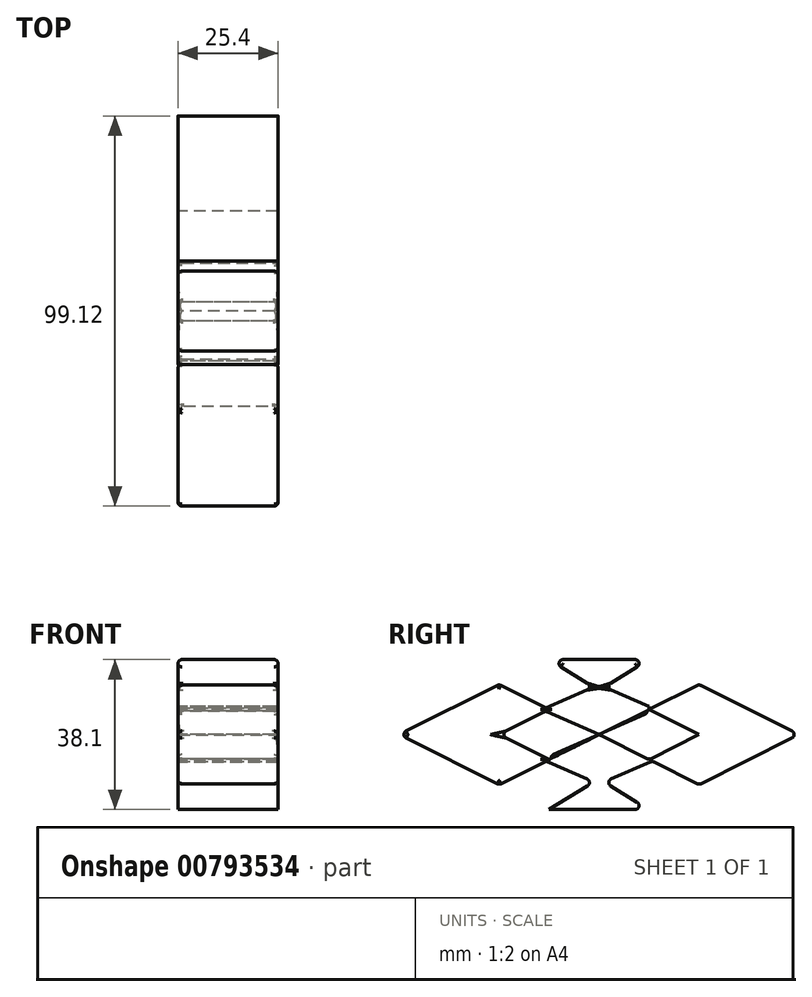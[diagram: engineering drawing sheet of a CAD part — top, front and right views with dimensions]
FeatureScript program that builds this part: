
annotation { "Feature Type Name" : "Feature", "Feature Type Description" : "" }
export const myFeature = defineFeature(function(context is Context, id is Id, definition is map)
    precondition{}
    {
        {
            var Q0;
            Q0=qCreatedBy(makeId("Right.planeOp"),FACE);
            var sketch = newSketch(context, id + "F0", { "sketchPlane" : qUnion([Q0])});
            skLineSegment(sketch, "E0", {"start": v(-25.4, 0) * mm, "end": v(-25.4, 12.7) * mm});
            skLineSegment(sketch, "E1.MirrorCS", {"start": v(-25.4, 0) * mm, "end": v(-25.4, -12.7) * mm});
            skLineSegment(sketch, "E2.1.0.0", {"start": v(0, 0) * mm, "end": v(0, 12.7) * mm});
            skLineSegment(sketch, "E2.1.0.1", {"start": v(0, 0) * mm, "end": v(0, -12.7) * mm});
            skLineSegment(sketch, "E2.2.0.0", {"start": v(25.4, 0) * mm, "end": v(25.4, 12.7) * mm});
            skLineSegment(sketch, "E2.2.0.1", {"start": v(25.4, 0) * mm, "end": v(25.4, -12.7) * mm});
            skLineSegment(sketch, "E3", {"start": v(-25.4, 12.7) * mm, "end": v(25.4, -12.7) * mm});
            skLineSegment(sketch, "E4", {"start": v(25.4, 12.7) * mm, "end": v(-25.4, -12.7) * mm});
            skLineSegment(sketch, "E5", {"start": v(-25.4, 0) * mm, "end": v(0, 12.7) * mm});
            skLineSegment(sketch, "E6", {"start": v(0, 12.7) * mm, "end": v(25.4, 0) * mm});
            skLineSegment(sketch, "E7", {"start": v(25.4, 0) * mm, "end": v(0, -12.7) * mm});
            skLineSegment(sketch, "E8", {"start": v(0, -12.7) * mm, "end": v(-25.4, 0) * mm});
            skLineSegment(sketch, "E9", {"start": v(-12.7, 6.35) * mm, "end": v(-12.7, 19.05) * mm});
            skLineSegment(sketch, "E10", {"start": v(12.7, 6.35) * mm, "end": v(12.7, 19.05) * mm});
            skLineSegment(sketch, "E11.MirrorCS", {"start": v(-12.7, -6.35) * mm, "end": v(-12.7, -19.05) * mm});
            skLineSegment(sketch, "E12.MirrorCS", {"start": v(12.7, -6.35) * mm, "end": v(12.7, -19.05) * mm});
            skLineSegment(sketch, "E13", {"start": v(-12.7, 19.05) * mm, "end": v(-25.4, 12.7) * mm});
            skLineSegment(sketch, "E14", {"start": v(-25.4, -12.7) * mm, "end": v(-12.7, -19.05) * mm});
            skLineSegment(sketch, "E15", {"start": v(12.7, -19.05) * mm, "end": v(25.4, -12.7) * mm});
            skLineSegment(sketch, "E16", {"start": v(12.7, 19.05) * mm, "end": v(25.4, 12.7) * mm});
            skLineSegment(sketch, "E17", {"start": v(-12.7, 19.05) * mm, "end": v(12.7, 19.05) * mm});
            skLineSegment(sketch, "E18", {"start": v(0, 12.7) * mm, "end": v(-12.7, 19.05) * mm});
            skLineSegment(sketch, "E19", {"start": v(0, 12.7) * mm, "end": v(12.7, 19.05) * mm});
            skLineSegment(sketch, "E20", {"start": v(0, -12.7) * mm, "end": v(-12.7, -19.05) * mm});
            skLineSegment(sketch, "E21", {"start": v(0, -12.7) * mm, "end": v(12.7, -19.05) * mm});
            skLineSegment(sketch, "E22", {"start": v(12.7, -19.05) * mm, "end": v(-12.7, -19.05) * mm});
            skLineSegment(sketch, "E23", {"start": v(-25.4, 12.7) * mm, "end": v(-50.8, 0) * mm});
            skLineSegment(sketch, "E24", {"start": v(-50.8, 0) * mm, "end": v(-25.4, -12.7) * mm});
            skLineSegment(sketch, "E25", {"start": v(25.4, 12.7) * mm, "end": v(50.8, 0) * mm});
            skLineSegment(sketch, "E26", {"start": v(50.8, 0) * mm, "end": v(25.4, -12.7) * mm});
            skLineSegment(sketch, "E27", {"start": v(50.8, 0) * mm, "end": v(-50.8, 0) * mm});
            skLineSegment(sketch, "E28", {"start": v(12.7, 19.05) * mm, "end": v(1.3, 12.05) * mm});
            skLineSegment(sketch, "E29.MirrorCS", {"start": v(-12.7, 19.05) * mm, "end": v(-1.3, 12.05) * mm});
            skLineSegment(sketch, "E30.MirrorCS", {"start": v(12.7, -19.05) * mm, "end": v(1.3, -12.05) * mm});
            skLineSegment(sketch, "E31.MirrorCS", {"start": v(-12.7, -19.05) * mm, "end": v(-1.3, -12.05) * mm});
            skLineSegment(sketch, "E32", {"start": v(0, 0) * mm, "end": v(13.53, 5.93) * mm});
            skLineSegment(sketch, "E33", {"start": v(1.3, 12.05) * mm, "end": v(13.53, 6.77) * mm});
            skLineSegment(sketch, "E34.MirrorCS", {"start": v(-1.3, 12.05) * mm, "end": v(-13.53, 6.77) * mm});
            skLineSegment(sketch, "E35.MirrorCS", {"start": v(0, 0) * mm, "end": v(-13.53, 5.93) * mm});
            skLineSegment(sketch, "E36.MirrorCS", {"start": v(0, 0) * mm, "end": v(13.53, -5.93) * mm});
            skLineSegment(sketch, "E37.MirrorCS", {"start": v(1.3, -12.05) * mm, "end": v(13.53, -6.77) * mm});
            skLineSegment(sketch, "E38.MirrorCS", {"start": v(0, 0) * mm, "end": v(-13.53, -5.93) * mm});
            skLineSegment(sketch, "E39.MirrorCS", {"start": v(-1.3, -12.05) * mm, "end": v(-13.53, -6.77) * mm});
            skSolve(sketch);
        }
        {
            var Q0;
            {var subQ0=sQuery(id+"F0.wireOp",EDGE,"E1.MirrorCS");Q0=makeQuery(id+"F0.imprint","IMPRINT",FACE,{"disambiguationData":[TD([[makeQuery(id+"F0.imprint","IMPRINT",EDGE,{"derivedFrom":subQ0}),-1.0]])]});}
            var Q1;
            {var subQ0=sQuery(id+"F0.wireOp",EDGE,"E2.2.0.0");Q1=makeQuery(id+"F0.imprint","IMPRINT",FACE,{"disambiguationData":[TD([[makeQuery(id+"F0.imprint","IMPRINT",EDGE,{"derivedFrom":subQ0}),-1.0]])]});}
            var Q2;
            {var subQ0=sQuery(id+"F0.wireOp",EDGE,"E2.2.0.0");Q2=makeQuery(id+"F0.imprint","IMPRINT",FACE,{"disambiguationData":[TD([[makeQuery(id+"F0.imprint","IMPRINT",EDGE,{"derivedFrom":subQ0}),1.0]])]});}
            var Q3;
            {var subQ0=sQuery(id+"F0.wireOp",EDGE,"E2.1.0.0");Q3=makeQuery(id+"F0.imprint","IMPRINT",FACE,{"disambiguationData":[TD([[makeQuery(id+"F0.imprint","IMPRINT",EDGE,{"derivedFrom":subQ0}),-1.0]])]});}
            var Q4;
            {var subQ0=sQuery(id+"F0.wireOp",EDGE,"E2.1.0.0");Q4=makeQuery(id+"F0.imprint","IMPRINT",FACE,{"disambiguationData":[TD([[makeQuery(id+"F0.imprint","IMPRINT",EDGE,{"derivedFrom":subQ0}),1.0]])]});}
            var Q5;
            {var subQ0=sQuery(id+"F0.wireOp",EDGE,"E0");Q5=makeQuery(id+"F0.imprint","IMPRINT",FACE,{"disambiguationData":[TD([[makeQuery(id+"F0.imprint","IMPRINT",EDGE,{"derivedFrom":subQ0}),-1.0]])]});}
            var Q6;
            {var subQ0=sQuery(id+"F0.wireOp",EDGE,"E1.MirrorCS");Q6=makeQuery(id+"F0.imprint","IMPRINT",FACE,{"disambiguationData":[TD([[makeQuery(id+"F0.imprint","IMPRINT",EDGE,{"derivedFrom":subQ0}),1.0]])]});}
            var Q7;
            {var subQ0=sQuery(id+"F0.wireOp",EDGE,"E2.1.0.1");Q7=makeQuery(id+"F0.imprint","IMPRINT",FACE,{"disambiguationData":[TD([[makeQuery(id+"F0.imprint","IMPRINT",EDGE,{"derivedFrom":subQ0}),1.0]])]});}
            var Q8;
            {var subQ0=sQuery(id+"F0.wireOp",EDGE,"E2.2.0.1");Q8=makeQuery(id+"F0.imprint","IMPRINT",FACE,{"disambiguationData":[TD([[makeQuery(id+"F0.imprint","IMPRINT",EDGE,{"derivedFrom":subQ0}),-1.0]])]});}
            var Q9;
            Q9=makeQuery(id+"F0.imprint","IMPRINT",FACE,{"disambiguationData":[TD([[makeQuery(id+"F0.imprint","IMPRINT",EDGE,{"derivedFrom":sQuery(id+"F0.wireOp",EDGE,"E20")}),1.0]])]});
            var Q10;
            Q10=makeQuery(id+"F0.imprint","IMPRINT",FACE,{"disambiguationData":[TD([[makeQuery(id+"F0.imprint","IMPRINT",EDGE,{"derivedFrom":sQuery(id+"F0.wireOp",EDGE,"E17")}),-1.0]])]});
            var Q11;
            {var subQ0=sQuery(id+"F0.wireOp",EDGE,"E0");Q11=makeQuery(id+"F0.imprint","IMPRINT",FACE,{"disambiguationData":[TD([[makeQuery(id+"F0.imprint","IMPRINT",EDGE,{"derivedFrom":subQ0}),1.0]])]});}
            var Q12;
            {var subQ0=sQuery(id+"F0.wireOp",EDGE,"E2.2.0.1");Q12=makeQuery(id+"F0.imprint","IMPRINT",FACE,{"disambiguationData":[TD([[makeQuery(id+"F0.imprint","IMPRINT",EDGE,{"derivedFrom":subQ0}),1.0]])]});}
            var Q13;
            {var subQ0=sQuery(id+"F0.wireOp",EDGE,"E19");Q13=makeQuery(id+"F0.imprint","IMPRINT",FACE,{"disambiguationData":[TD([[makeQuery(id+"F0.imprint","IMPRINT",EDGE,{"derivedFrom":subQ0}),-1.0]])]});}
            var Q14;
            {var subQ0=sQuery(id+"F0.wireOp",EDGE,"E18");Q14=makeQuery(id+"F0.imprint","IMPRINT",FACE,{"disambiguationData":[TD([[makeQuery(id+"F0.imprint","IMPRINT",EDGE,{"derivedFrom":subQ0}),1.0]])]});}
            var Q15;
            {var subQ0=sQuery(id+"F0.wireOp",EDGE,"E20");Q15=makeQuery(id+"F0.imprint","IMPRINT",FACE,{"disambiguationData":[TD([[makeQuery(id+"F0.imprint","IMPRINT",EDGE,{"derivedFrom":subQ0}),-1.0]])]});}
            var Q16;
            {var subQ1=sQuery(id+"F0.wireOp",EDGE,"E3");var subQ3=sQuery(id+"F0.wireOp",EDGE,"E37.MirrorCS");var subQ4=makeQuery(id+"F0.imprint","INTERSECT",VERTEX,{"derivedFrom":[subQ1,subQ3]});Q16=makeQuery(id+"F0.imprint","IMPRINT",FACE,{"disambiguationData":[TD([[makeQuery(id+"F0.imprint","IMPRINT",EDGE,{"disambiguationData":[TD([[subQ4,1.0]])],"derivedFrom":subQ3}),1.0]])]});}
            var Q17;
            {var subQ0=sQuery(id+"F0.wireOp",EDGE,"E9");var subQ3=sQuery(id+"F0.wireOp",EDGE,"E34.MirrorCS");var subQ5=makeQuery(id+"F0.imprint","INTERSECT",VERTEX,{"derivedFrom":[subQ0,subQ3]});Q17=makeQuery(id+"F0.imprint","IMPRINT",FACE,{"disambiguationData":[TD([[makeQuery(id+"F0.imprint","IMPRINT",EDGE,{"disambiguationData":[TD([[subQ5,1.0]])],"derivedFrom":subQ0}),-1.0]])]});}
            var Q18;
            {var subQ1=sQuery(id+"F0.wireOp",EDGE,"E3");var subQ3=sQuery(id+"F0.wireOp",EDGE,"E34.MirrorCS");var subQ4=makeQuery(id+"F0.imprint","INTERSECT",VERTEX,{"derivedFrom":[subQ1,subQ3]});Q18=makeQuery(id+"F0.imprint","IMPRINT",FACE,{"disambiguationData":[TD([[makeQuery(id+"F0.imprint","IMPRINT",EDGE,{"disambiguationData":[TD([[subQ4,1.0]])],"derivedFrom":subQ3}),1.0]])]});}
            var Q19;
            {var subQ0=sQuery(id+"F0.wireOp",EDGE,"E35.MirrorCS");Q19=makeQuery(id+"F0.imprint","IMPRINT",FACE,{"disambiguationData":[TD([[makeQuery(id+"F0.imprint","IMPRINT",EDGE,{"derivedFrom":subQ0}),-1.0]])]});}
            var Q20;
            {var subQ0=sQuery(id+"F0.wireOp",EDGE,"E11.MirrorCS");var subQ3=sQuery(id+"F0.wireOp",EDGE,"E39.MirrorCS");var subQ5=makeQuery(id+"F0.imprint","INTERSECT",VERTEX,{"derivedFrom":[subQ0,subQ3]});Q20=makeQuery(id+"F0.imprint","IMPRINT",FACE,{"disambiguationData":[TD([[makeQuery(id+"F0.imprint","IMPRINT",EDGE,{"disambiguationData":[TD([[subQ5,1.0]])],"derivedFrom":subQ0}),1.0]])]});}
            var Q21;
            {var subQ0=sQuery(id+"F0.wireOp",EDGE,"E21");Q21=makeQuery(id+"F0.imprint","IMPRINT",FACE,{"disambiguationData":[TD([[makeQuery(id+"F0.imprint","IMPRINT",EDGE,{"derivedFrom":subQ0}),1.0]])]});}
            var Q22;
            {var subQ0=sQuery(id+"F0.wireOp",EDGE,"E12.MirrorCS");var subQ3=sQuery(id+"F0.wireOp",EDGE,"E37.MirrorCS");var subQ5=makeQuery(id+"F0.imprint","INTERSECT",VERTEX,{"derivedFrom":[subQ0,subQ3]});Q22=makeQuery(id+"F0.imprint","IMPRINT",FACE,{"disambiguationData":[TD([[makeQuery(id+"F0.imprint","IMPRINT",EDGE,{"disambiguationData":[TD([[subQ5,1.0]])],"derivedFrom":subQ0}),-1.0]])]});}
            var Q23;
            {var subQ0=sQuery(id+"F0.wireOp",EDGE,"E36.MirrorCS");Q23=makeQuery(id+"F0.imprint","IMPRINT",FACE,{"disambiguationData":[TD([[makeQuery(id+"F0.imprint","IMPRINT",EDGE,{"derivedFrom":subQ0}),-1.0]])]});}
            var Q24;
            {var subQ0=sQuery(id+"F0.wireOp",EDGE,"E10");var subQ3=sQuery(id+"F0.wireOp",EDGE,"E33");var subQ5=makeQuery(id+"F0.imprint","INTERSECT",VERTEX,{"derivedFrom":[subQ0,subQ3]});Q24=makeQuery(id+"F0.imprint","IMPRINT",FACE,{"disambiguationData":[TD([[makeQuery(id+"F0.imprint","IMPRINT",EDGE,{"disambiguationData":[TD([[subQ5,1.0]])],"derivedFrom":subQ0}),1.0]])]});}
            var Q25;
            {var subQ0=sQuery(id+"F0.wireOp",EDGE,"E2.1.0.1");Q25=makeQuery(id+"F0.imprint","IMPRINT",FACE,{"disambiguationData":[TD([[makeQuery(id+"F0.imprint","IMPRINT",EDGE,{"derivedFrom":subQ0}),-1.0]])]});}
            extrude(context, id + "F1", {"entities" : qUnion([Q0, Q1, Q2, Q3, Q4, Q5, Q6, Q7, Q8, Q9, Q10, Q11, Q12, Q13, Q14, Q15, Q16, Q17, Q18, Q19, Q20, Q21, Q22, Q23, Q24, Q25]), "depth" : 25.4 * mm, "offsetDistance" : 25.4 * mm});
        }
        {
            var Q0;
            {var subQ1=sQuery(id+"F0.wireOp",EDGE,"E4");var subQ3=sQuery(id+"F0.wireOp",EDGE,"E39.MirrorCS");var subQ4=makeQuery(id+"F0.imprint","INTERSECT",VERTEX,{"derivedFrom":[subQ1,subQ3]});Q0=makeQuery(id+"F0.imprint","IMPRINT",FACE,{"disambiguationData":[TD([[makeQuery(id+"F0.imprint","IMPRINT",EDGE,{"disambiguationData":[TD([[subQ4,1.0]])],"derivedFrom":subQ3}),-1.0]])]});}
            var Q1;
            {var subQ0=sQuery(id+"F0.wireOp",EDGE,"E38.MirrorCS");Q1=makeQuery(id+"F0.imprint","IMPRINT",FACE,{"disambiguationData":[TD([[makeQuery(id+"F0.imprint","IMPRINT",EDGE,{"derivedFrom":subQ0}),1.0]])]});}
            var Q2;
            {var subQ1=sQuery(id+"F0.wireOp",EDGE,"E4");var subQ3=sQuery(id+"F0.wireOp",EDGE,"E33");var subQ4=makeQuery(id+"F0.imprint","INTERSECT",VERTEX,{"derivedFrom":[subQ1,subQ3]});Q2=makeQuery(id+"F0.imprint","IMPRINT",FACE,{"disambiguationData":[TD([[makeQuery(id+"F0.imprint","IMPRINT",EDGE,{"disambiguationData":[TD([[subQ4,1.0]])],"derivedFrom":subQ3}),-1.0]])]});}
            var Q3;
            {var subQ0=sQuery(id+"F0.wireOp",EDGE,"E32");Q3=makeQuery(id+"F0.imprint","IMPRINT",FACE,{"disambiguationData":[TD([[makeQuery(id+"F0.imprint","IMPRINT",EDGE,{"derivedFrom":subQ0}),1.0]])]});}
            extrude(context, id + "F2", {"entities" : qUnion([Q0, Q1, Q2, Q3]), "depth" : 25.4 * mm, "offsetDistance" : 25.4 * mm});
        }
        {
            var Q0;
            Q0=makeQuery(id+"F2.opExtrude","CAP_EDGE",EDGE,{"disambiguationData":[OSD([sQuery(id+"F0.wireOp",EDGE,"E38.MirrorCS")])],"isStart":false});
            var Q1;
            Q1=makeQuery(id+"F1.opExtrude","CAP_EDGE",EDGE,{"disambiguationData":[OSD([sQuery(id+"F0.wireOp",EDGE,"E39.MirrorCS")])],"isStart":false});
            var Q2;
            {var subQ0=sQuery(id+"F0.wireOp",EDGE,"E4");var subQ1=makeQuery(id+"F0.imprint","INTERSECT",VERTEX,{"derivedFrom":[subQ0,sQuery(id+"F0.wireOp",EDGE,"E39.MirrorCS")]});Q2=makeQuery(id+"F1.opExtrude","CAP_EDGE",EDGE,{"disambiguationData":[OSD([subQ0]),TDD([makeQuery(id+"F0.imprint","IMPRINT",EDGE,{"disambiguationData":[TD([[subQ1,1.0]])],"derivedFrom":subQ0}),makeQuery(id+"F0.imprint","IMPRINT",EDGE,{"disambiguationData":[TD([[subQ1,-1.0]])],"derivedFrom":subQ0})])],"isStart":false});}
            var Q3;
            Q3=makeQuery(id+"F1.opExtrude","CAP_EDGE",EDGE,{"disambiguationData":[OSD([sQuery(id+"F0.wireOp",EDGE,"E8")])],"isStart":false});
            var Q4;
            Q4=makeQuery(id+"F1.opExtrude","CAP_EDGE",EDGE,{"disambiguationData":[OSD([sQuery(id+"F0.wireOp",EDGE,"E5")])],"isStart":false});
            var Q5;
            Q5=makeQuery(id+"F1.opExtrude","CAP_EDGE",EDGE,{"disambiguationData":[OSD([sQuery(id+"F0.wireOp",EDGE,"E35.MirrorCS")])],"isStart":false});
            var Q6;
            Q6=makeQuery(id+"F1.opExtrude","CAP_EDGE",EDGE,{"disambiguationData":[OSD([sQuery(id+"F0.wireOp",EDGE,"E34.MirrorCS")])],"isStart":false});
            var Q7;
            {var subQ0=sQuery(id+"F0.wireOp",EDGE,"E3");Q7=makeQuery(id+"F1.opExtrude","CAP_EDGE",EDGE,{"disambiguationData":[OSD([subQ0]),TDD([makeQuery(id+"F0.imprint","IMPRINT",EDGE,{"disambiguationData":[TD([[makeQuery(id+"F0.imprint","INTERSECT",VERTEX,{"derivedFrom":[subQ0,sQuery(id+"F0.wireOp",EDGE,"E34.MirrorCS")]}),1.0]])],"derivedFrom":subQ0})])],"isStart":false});}
            var Q8;
            Q8=makeQuery(id+"F1.opExtrude","CAP_EDGE",EDGE,{"disambiguationData":[OSD([sQuery(id+"F0.wireOp",EDGE,"E23")])],"isStart":false});
            var Q9;
            Q9=makeQuery(id+"F1.opExtrude","CAP_EDGE",EDGE,{"disambiguationData":[OSD([sQuery(id+"F0.wireOp",EDGE,"E24")])],"isStart":false});
            var Q10;
            Q10=makeQuery(id+"F1.opExtrude","CAP_EDGE",EDGE,{"disambiguationData":[OSD([sQuery(id+"F0.wireOp",EDGE,"E29.MirrorCS")])],"isStart":false});
            var Q11;
            Q11=makeQuery(id+"F1.opExtrude","CAP_EDGE",EDGE,{"disambiguationData":[OSD([sQuery(id+"F0.wireOp",EDGE,"E17")])],"isStart":false});
            var Q12;
            Q12=makeQuery(id+"F1.opExtrude","CAP_EDGE",EDGE,{"disambiguationData":[OSD([sQuery(id+"F0.wireOp",EDGE,"E28")])],"isStart":false});
            var Q13;
            Q13=makeQuery(id+"F1.opExtrude","CAP_EDGE",EDGE,{"disambiguationData":[OSD([sQuery(id+"F0.wireOp",EDGE,"E33")])],"isStart":false});
            var Q14;
            {var subQ0=sQuery(id+"F0.wireOp",EDGE,"E4");var subQ1=makeQuery(id+"F0.imprint","INTERSECT",VERTEX,{"derivedFrom":[subQ0,sQuery(id+"F0.wireOp",EDGE,"E33")]});Q14=makeQuery(id+"F1.opExtrude","CAP_EDGE",EDGE,{"disambiguationData":[OSD([subQ0]),TDD([makeQuery(id+"F0.imprint","IMPRINT",EDGE,{"disambiguationData":[TD([[subQ1,1.0]])],"derivedFrom":subQ0}),makeQuery(id+"F0.imprint","IMPRINT",EDGE,{"disambiguationData":[TD([[subQ1,-1.0]])],"derivedFrom":subQ0})])],"isStart":false});}
            var Q15;
            Q15=makeQuery(id+"F1.opExtrude","CAP_EDGE",EDGE,{"disambiguationData":[OSD([sQuery(id+"F0.wireOp",EDGE,"E25")])],"isStart":false});
            var Q16;
            Q16=makeQuery(id+"F1.opExtrude","CAP_EDGE",EDGE,{"disambiguationData":[OSD([sQuery(id+"F0.wireOp",EDGE,"E7")])],"isStart":false});
            var Q17;
            Q17=makeQuery(id+"F1.opExtrude","CAP_EDGE",EDGE,{"disambiguationData":[OSD([sQuery(id+"F0.wireOp",EDGE,"E6")])],"isStart":false});
            var Q18;
            Q18=makeQuery(id+"F1.opExtrude","CAP_EDGE",EDGE,{"disambiguationData":[OSD([sQuery(id+"F0.wireOp",EDGE,"E26")])],"isStart":false});
            var Q19;
            {var subQ0=sQuery(id+"F0.wireOp",EDGE,"E3");Q19=makeQuery(id+"F1.opExtrude","CAP_EDGE",EDGE,{"disambiguationData":[OSD([subQ0]),TDD([makeQuery(id+"F0.imprint","IMPRINT",EDGE,{"disambiguationData":[TD([[makeQuery(id+"F0.imprint","INTERSECT",VERTEX,{"derivedFrom":[subQ0,sQuery(id+"F0.wireOp",EDGE,"E37.MirrorCS")]}),-1.0]])],"derivedFrom":subQ0})])],"isStart":false});}
            var Q20;
            Q20=makeQuery(id+"F1.opExtrude","CAP_EDGE",EDGE,{"disambiguationData":[OSD([sQuery(id+"F0.wireOp",EDGE,"E37.MirrorCS")])],"isStart":false});
            var Q21;
            Q21=makeQuery(id+"F1.opExtrude","CAP_EDGE",EDGE,{"disambiguationData":[OSD([sQuery(id+"F0.wireOp",EDGE,"E30.MirrorCS")])],"isStart":false});
            var Q22;
            Q22=makeQuery(id+"F1.opExtrude","CAP_EDGE",EDGE,{"disambiguationData":[OSD([sQuery(id+"F0.wireOp",EDGE,"E22")])],"isStart":false});
            var Q23;
            Q23=makeQuery(id+"F1.opExtrude","CAP_EDGE",EDGE,{"disambiguationData":[OSD([sQuery(id+"F0.wireOp",EDGE,"E31.MirrorCS")])],"isStart":false});
            var Q24;
            Q24=makeQuery(id+"F2.opExtrude","CAP_EDGE",EDGE,{"disambiguationData":[OSD([sQuery(id+"F0.wireOp",EDGE,"E32")])],"isStart":false});
            var Q25;
            Q25=makeQuery(id+"F1.opExtrude","CAP_EDGE",EDGE,{"disambiguationData":[OSD([sQuery(id+"F0.wireOp",EDGE,"E36.MirrorCS")])],"isStart":false});
            var Q26;
            Q26=makeQuery(id+"F2.opExtrude","CAP_EDGE",EDGE,{"disambiguationData":[OSD([sQuery(id+"F0.wireOp",EDGE,"E38.MirrorCS")])],"isStart":true});
            var Q27;
            Q27=makeQuery(id+"F1.opExtrude","CAP_EDGE",EDGE,{"disambiguationData":[OSD([sQuery(id+"F0.wireOp",EDGE,"E35.MirrorCS")])],"isStart":true});
            var Q28;
            Q28=makeQuery(id+"F1.opExtrude","CAP_EDGE",EDGE,{"disambiguationData":[OSD([sQuery(id+"F0.wireOp",EDGE,"E5")])],"isStart":true});
            var Q29;
            Q29=makeQuery(id+"F1.opExtrude","CAP_EDGE",EDGE,{"disambiguationData":[OSD([sQuery(id+"F0.wireOp",EDGE,"E8")])],"isStart":true});
            var Q30;
            Q30=makeQuery(id+"F1.opExtrude","CAP_EDGE",EDGE,{"disambiguationData":[OSD([sQuery(id+"F0.wireOp",EDGE,"E36.MirrorCS")])],"isStart":true});
            var Q31;
            Q31=makeQuery(id+"F2.opExtrude","CAP_EDGE",EDGE,{"disambiguationData":[OSD([sQuery(id+"F0.wireOp",EDGE,"E32")])],"isStart":true});
            var Q32;
            Q32=makeQuery(id+"F1.opExtrude","CAP_EDGE",EDGE,{"disambiguationData":[OSD([sQuery(id+"F0.wireOp",EDGE,"E7")])],"isStart":true});
            var Q33;
            Q33=makeQuery(id+"F1.opExtrude","CAP_EDGE",EDGE,{"disambiguationData":[OSD([sQuery(id+"F0.wireOp",EDGE,"E6")])],"isStart":true});
            var Q34;
            Q34=makeQuery(id+"F1.opExtrude","CAP_EDGE",EDGE,{"disambiguationData":[OSD([sQuery(id+"F0.wireOp",EDGE,"E33")])],"isStart":true});
            var Q35;
            {var subQ0=sQuery(id+"F0.wireOp",EDGE,"E4");var subQ1=makeQuery(id+"F0.imprint","INTERSECT",VERTEX,{"derivedFrom":[subQ0,sQuery(id+"F0.wireOp",EDGE,"E33")]});Q35=makeQuery(id+"F1.opExtrude","CAP_EDGE",EDGE,{"disambiguationData":[OSD([subQ0]),TDD([makeQuery(id+"F0.imprint","IMPRINT",EDGE,{"disambiguationData":[TD([[subQ1,1.0]])],"derivedFrom":subQ0}),makeQuery(id+"F0.imprint","IMPRINT",EDGE,{"disambiguationData":[TD([[subQ1,-1.0]])],"derivedFrom":subQ0})])],"isStart":true});}
            var Q36;
            Q36=makeQuery(id+"F1.opExtrude","CAP_EDGE",EDGE,{"disambiguationData":[OSD([sQuery(id+"F0.wireOp",EDGE,"E28")])],"isStart":true});
            var Q37;
            Q37=makeQuery(id+"F1.opExtrude","CAP_EDGE",EDGE,{"disambiguationData":[OSD([sQuery(id+"F0.wireOp",EDGE,"E37.MirrorCS")])],"isStart":true});
            var Q38;
            {var subQ0=sQuery(id+"F0.wireOp",EDGE,"E3");Q38=makeQuery(id+"F1.opExtrude","CAP_EDGE",EDGE,{"disambiguationData":[OSD([subQ0]),TDD([makeQuery(id+"F0.imprint","IMPRINT",EDGE,{"disambiguationData":[TD([[makeQuery(id+"F0.imprint","INTERSECT",VERTEX,{"derivedFrom":[subQ0,sQuery(id+"F0.wireOp",EDGE,"E37.MirrorCS")]}),-1.0]])],"derivedFrom":subQ0})])],"isStart":true});}
            var Q39;
            Q39=makeQuery(id+"F1.opExtrude","CAP_FACE",FACE,{"disambiguationData":[OSD([sQuery(id+"F0.wireOp",EDGE,"E3"),sQuery(id+"F0.wireOp",EDGE,"E4"),sQuery(id+"F0.wireOp",EDGE,"E6"),sQuery(id+"F0.wireOp",EDGE,"E7"),sQuery(id+"F0.wireOp",EDGE,"E11.MirrorCS"),sQuery(id+"F0.wireOp",EDGE,"E22"),sQuery(id+"F0.wireOp",EDGE,"E25"),sQuery(id+"F0.wireOp",EDGE,"E26"),sQuery(id+"F0.wireOp",EDGE,"E30.MirrorCS"),sQuery(id+"F0.wireOp",EDGE,"E31.MirrorCS"),sQuery(id+"F0.wireOp",EDGE,"E37.MirrorCS"),sQuery(id+"F0.wireOp",EDGE,"E36.MirrorCS"),sQuery(id+"F0.wireOp",EDGE,"E39.MirrorCS")])],"isStart":true});
            var Q40;
            Q40=makeQuery(id+"F1.opExtrude","CAP_EDGE",EDGE,{"disambiguationData":[OSD([sQuery(id+"F0.wireOp",EDGE,"E29.MirrorCS")])],"isStart":true});
            var Q41;
            Q41=makeQuery(id+"F1.opExtrude","CAP_EDGE",EDGE,{"disambiguationData":[OSD([sQuery(id+"F0.wireOp",EDGE,"E34.MirrorCS")])],"isStart":true});
            var Q42;
            {var subQ0=sQuery(id+"F0.wireOp",EDGE,"E3");Q42=makeQuery(id+"F1.opExtrude","CAP_EDGE",EDGE,{"disambiguationData":[OSD([subQ0]),TDD([makeQuery(id+"F0.imprint","IMPRINT",EDGE,{"disambiguationData":[TD([[makeQuery(id+"F0.imprint","INTERSECT",VERTEX,{"derivedFrom":[subQ0,sQuery(id+"F0.wireOp",EDGE,"E34.MirrorCS")]}),1.0]])],"derivedFrom":subQ0})])],"isStart":true});}
            var Q43;
            {var subQ0=sQuery(id+"F0.wireOp",EDGE,"E4");var subQ1=makeQuery(id+"F0.imprint","INTERSECT",VERTEX,{"derivedFrom":[subQ0,sQuery(id+"F0.wireOp",EDGE,"E39.MirrorCS")]});Q43=makeQuery(id+"F1.opExtrude","CAP_EDGE",EDGE,{"disambiguationData":[OSD([subQ0]),TDD([makeQuery(id+"F0.imprint","IMPRINT",EDGE,{"disambiguationData":[TD([[subQ1,1.0]])],"derivedFrom":subQ0}),makeQuery(id+"F0.imprint","IMPRINT",EDGE,{"disambiguationData":[TD([[subQ1,-1.0]])],"derivedFrom":subQ0})])],"isStart":true});}
            var Q44;
            Q44=makeQuery(id+"F1.opExtrude","CAP_EDGE",EDGE,{"disambiguationData":[OSD([sQuery(id+"F0.wireOp",EDGE,"E24")])],"isStart":true});
            var Q45;
            Q45=makeQuery(id+"F1.opExtrude","CAP_EDGE",EDGE,{"disambiguationData":[OSD([sQuery(id+"F0.wireOp",EDGE,"E23")])],"isStart":true});
            fillet(context, id + "F3", {"entities" : qUnion([Q0, Q1, Q2, Q3, Q4, Q5, Q6, Q7, Q8, Q9, Q10, Q11, Q12, Q13, Q14, Q15, Q16, Q17, Q18, Q19, Q20, Q21, Q22, Q23, Q24, Q25, Q26, Q27, Q28, Q29, Q30, Q31, Q32, Q33, Q34, Q35, Q36, Q37, Q38, Q39, Q40, Q41, Q42, Q43, Q44, Q45]), "radius" : 1 * mm, "tangentPropagation" : true, "allowEdgeOverflow" : false});
        }
        {
            var Q0;
            Q0=makeQuery(id+"F1.opExtrude","SWEPT_EDGE",EDGE,{"disambiguationData":[OSD([sQuery(id+"F0.wireOp",EDGE,"E12.MirrorCS"),sQuery(id+"F0.wireOp",EDGE,"E15"),sQuery(id+"F0.wireOp",EDGE,"E21"),sQuery(id+"F0.wireOp",EDGE,"E22"),sQuery(id+"F0.wireOp",EDGE,"E30.MirrorCS")])]});
            var Q1;
            Q1=makeQuery(id+"F1.opExtrude","SWEPT_EDGE",EDGE,{"disambiguationData":[OSD([sQuery(id+"F0.wireOp",EDGE,"E3"),sQuery(id+"F0.wireOp",EDGE,"E37.MirrorCS")])]});
            var Q2;
            Q2=makeQuery(id+"F1.opExtrude","SWEPT_EDGE",EDGE,{"disambiguationData":[OSD([sQuery(id+"F0.wireOp",EDGE,"E7"),sQuery(id+"F0.wireOp",EDGE,"E30.MirrorCS"),sQuery(id+"F0.wireOp",EDGE,"E37.MirrorCS")])]});
            var Q3;
            Q3=makeQuery(id+"F1.opExtrude","SWEPT_EDGE",EDGE,{"disambiguationData":[OSD([sQuery(id+"F0.wireOp",EDGE,"E8"),sQuery(id+"F0.wireOp",EDGE,"E31.MirrorCS"),sQuery(id+"F0.wireOp",EDGE,"E39.MirrorCS")])]});
            var Q4;
            Q4=makeQuery(id+"F2.opExtrude","SWEPT_EDGE",EDGE,{"disambiguationData":[OSD([sQuery(id+"F0.wireOp",EDGE,"E6"),sQuery(id+"F0.wireOp",EDGE,"E32")])]});
            var Q5;
            Q5=makeQuery(id+"F1.opExtrude","SWEPT_EDGE",EDGE,{"disambiguationData":[OSD([sQuery(id+"F0.wireOp",EDGE,"E7"),sQuery(id+"F0.wireOp",EDGE,"E36.MirrorCS")])]});
            var Q6;
            {var subQ0=sQuery(id+"F0.wireOp",EDGE,"E4");var subQ1=makeQuery(id+"F0.imprint","INTERSECT",VERTEX,{"derivedFrom":[subQ0,sQuery(id+"F0.wireOp",EDGE,"E33")]});var subQ2=makeQuery(id+"F0.imprint","IMPRINT",EDGE,{"disambiguationData":[TD([[subQ1,-1.0]])],"derivedFrom":subQ0});var subQ3=makeQuery(id+"F0.imprint","IMPRINT",EDGE,{"disambiguationData":[TD([[subQ1,1.0]])],"derivedFrom":subQ0});Q6=makeQuery(id+"F3.opFillet","BLEND_EDGE",EDGE,{"blendedFrom":[makeQuery(id+"F1.opExtrude","CAP_EDGE",EDGE,{"disambiguationData":[OSD([subQ0]),TDD([subQ3,subQ2])],"isStart":false}),makeQuery(id+"F1.opExtrude","SWEPT_FACE",FACE,{"disambiguationData":[OSD([subQ0]),TDD([subQ3,subQ2])]})],"blendedInto":[makeQuery(id+"F1.opExtrude","SWEPT_FACE",FACE,{"disambiguationData":[OSD([subQ0]),TDD([subQ3,subQ2])]})]});}
            var Q7;
            Q7=makeQuery(id+"F2.opExtrude","SWEPT_EDGE",EDGE,{"disambiguationData":[OSD([sQuery(id+"F0.wireOp",EDGE,"E4"),sQuery(id+"F0.wireOp",EDGE,"E33")])]});
            var Q8;
            Q8=makeQuery(id+"F1.opExtrude","SWEPT_EDGE",EDGE,{"disambiguationData":[OSD([sQuery(id+"F0.wireOp",EDGE,"E6"),sQuery(id+"F0.wireOp",EDGE,"E28"),sQuery(id+"F0.wireOp",EDGE,"E33")])]});
            var Q9;
            Q9=makeQuery(id+"F1.opExtrude","SWEPT_EDGE",EDGE,{"disambiguationData":[OSD([sQuery(id+"F0.wireOp",EDGE,"E10"),sQuery(id+"F0.wireOp",EDGE,"E16"),sQuery(id+"F0.wireOp",EDGE,"E17"),sQuery(id+"F0.wireOp",EDGE,"E19"),sQuery(id+"F0.wireOp",EDGE,"E28")])]});
            var Q10;
            Q10=makeQuery(id+"F1.opExtrude","SWEPT_EDGE",EDGE,{"disambiguationData":[OSD([sQuery(id+"F0.wireOp",EDGE,"E2.2.0.0"),sQuery(id+"F0.wireOp",EDGE,"E4"),sQuery(id+"F0.wireOp",EDGE,"E16"),sQuery(id+"F0.wireOp",EDGE,"E25")])]});
            var Q11;
            Q11=makeQuery(id+"F1.opExtrude","SWEPT_EDGE",EDGE,{"disambiguationData":[OSD([sQuery(id+"F0.wireOp",EDGE,"E5"),sQuery(id+"F0.wireOp",EDGE,"E29.MirrorCS"),sQuery(id+"F0.wireOp",EDGE,"E34.MirrorCS")])]});
            var Q12;
            Q12=makeQuery(id+"F2.opExtrude","SWEPT_EDGE",EDGE,{"disambiguationData":[OSD([sQuery(id+"F0.wireOp",EDGE,"E8"),sQuery(id+"F0.wireOp",EDGE,"E38.MirrorCS")])]});
            var Q13;
            Q13=makeQuery(id+"F1.opExtrude","SWEPT_EDGE",EDGE,{"disambiguationData":[OSD([sQuery(id+"F0.wireOp",EDGE,"E0"),sQuery(id+"F0.wireOp",EDGE,"E1.MirrorCS"),sQuery(id+"F0.wireOp",EDGE,"E5"),sQuery(id+"F0.wireOp",EDGE,"E8"),sQuery(id+"F0.wireOp",EDGE,"E27")])]});
            var Q14;
            Q14=makeQuery(id+"F1.opExtrude","SWEPT_EDGE",EDGE,{"disambiguationData":[OSD([sQuery(id+"F0.wireOp",EDGE,"E5"),sQuery(id+"F0.wireOp",EDGE,"E35.MirrorCS")])]});
            var Q15;
            Q15=makeQuery(id+"F1.opExtrude","SWEPT_EDGE",EDGE,{"disambiguationData":[OSD([sQuery(id+"F0.wireOp",EDGE,"E2.1.0.0"),sQuery(id+"F0.wireOp",EDGE,"E2.1.0.1"),sQuery(id+"F0.wireOp",EDGE,"E3"),sQuery(id+"F0.wireOp",EDGE,"E4"),sQuery(id+"F0.wireOp",EDGE,"E27"),sQuery(id+"F0.wireOp",EDGE,"E32"),sQuery(id+"F0.wireOp",EDGE,"E35.MirrorCS"),sQuery(id+"F0.wireOp",EDGE,"E36.MirrorCS"),sQuery(id+"F0.wireOp",EDGE,"E38.MirrorCS")]),OD(0.0)]});
            var Q16;
            Q16=makeQuery(id+"F1.opExtrude","SWEPT_EDGE",EDGE,{"disambiguationData":[OSD([sQuery(id+"F0.wireOp",EDGE,"E1.MirrorCS"),sQuery(id+"F0.wireOp",EDGE,"E4"),sQuery(id+"F0.wireOp",EDGE,"E14"),sQuery(id+"F0.wireOp",EDGE,"E24")])]});
            var Q17;
            Q17=makeQuery(id+"F1.opExtrude","SWEPT_EDGE",EDGE,{"disambiguationData":[OSD([sQuery(id+"F0.wireOp",EDGE,"E23"),sQuery(id+"F0.wireOp",EDGE,"E24"),sQuery(id+"F0.wireOp",EDGE,"E27")])]});
            var Q18;
            Q18=makeQuery(id+"F1.opExtrude","SWEPT_EDGE",EDGE,{"disambiguationData":[OSD([sQuery(id+"F0.wireOp",EDGE,"E0"),sQuery(id+"F0.wireOp",EDGE,"E3"),sQuery(id+"F0.wireOp",EDGE,"E13"),sQuery(id+"F0.wireOp",EDGE,"E23")])]});
            var Q19;
            Q19=makeQuery(id+"F1.opExtrude","SWEPT_EDGE",EDGE,{"disambiguationData":[OSD([sQuery(id+"F0.wireOp",EDGE,"E25"),sQuery(id+"F0.wireOp",EDGE,"E26"),sQuery(id+"F0.wireOp",EDGE,"E27")])]});
            var Q20;
            Q20=makeQuery(id+"F1.opExtrude","SWEPT_EDGE",EDGE,{"disambiguationData":[OSD([sQuery(id+"F0.wireOp",EDGE,"E2.2.0.1"),sQuery(id+"F0.wireOp",EDGE,"E3"),sQuery(id+"F0.wireOp",EDGE,"E15"),sQuery(id+"F0.wireOp",EDGE,"E26")])]});
            fillet(context, id + "F4", {"entities" : qUnion([Q0, Q1, Q2, Q3, Q4, Q5, Q6, Q7, Q8, Q9, Q10, Q11, Q12, Q13, Q14, Q15, Q16, Q17, Q18, Q19, Q20]), "radius" : 1 * mm, "tangentPropagation" : true, "allowEdgeOverflow" : false});
        }
    });
